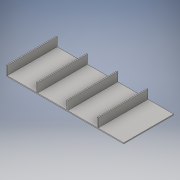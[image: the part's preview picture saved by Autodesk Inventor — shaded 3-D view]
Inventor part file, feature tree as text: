
AUTODESK INVENTOR PART (.ipt)
format: ipt  version: 2016 (Build 200138000, 138)  size: 133,632 bytes
history: native  units: in
note: dims shown in document units (in); Inventor stores cm internally (conversion verified against a paired STEP export)
features: extrude x5, sketch x5
ambient origin geometry x8: Origin, YZ Plane, XZ Plane, XY Plane, X Axis, Y Axis, Z Axis, Center Point
bodies: Solid1 (feature_tree)
feature tree (10):
  extrude  "Extrusion1"  Depth=0.063in
  extrude  "Extrusion2"  Depth=0.063in
  extrude  "Extrusion3"  Depth=0.063in
  extrude  "Extrusion4"  Depth=0.063in
  extrude  "Extrusion5"  Depth=0.063in
  sketch  "Sketch1"  dims[d0=8.0in d1=0.063in]
  sketch  "Sketch2"  dims[d2=3.4in d3=0.0in d4=0.063in]
  sketch  "Sketch3"  dims[d5=0.6in d6=0.0in d7=0.063in]
  sketch  "Sketch4"  dims[d8=0.6in d9=0.0in d10=0.063in]
  sketch  "Sketch5"  dims[d11=0.6in d12=0.0in d13=0.063in d14=0.6in d15=0.0in]
